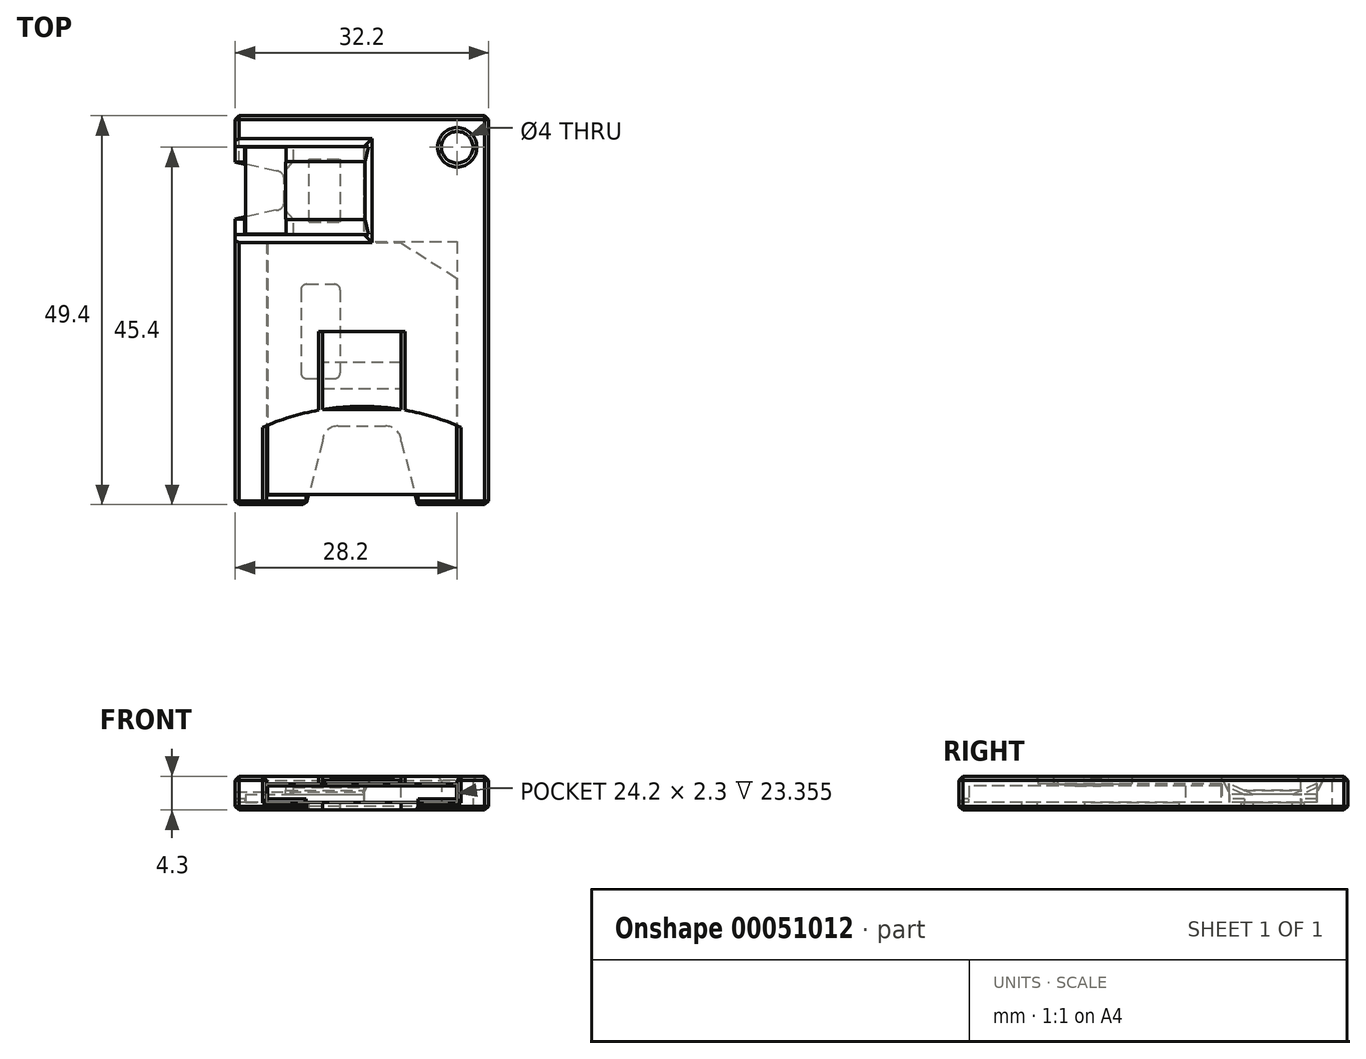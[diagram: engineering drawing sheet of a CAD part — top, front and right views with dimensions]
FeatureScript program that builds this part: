
annotation { "Feature Type Name" : "Feature", "Feature Type Description" : "" }
export const myFeature = defineFeature(function(context is Context, id is Id, definition is map)
    precondition{}
    {
        {
            var Q0;
            Q0=qCreatedBy(makeId("Top.planeOp"),FACE);
            var sketch = newSketch(context, id + "F0", { "sketchPlane" : qUnion([Q0])});
            skLineSegment(sketch, "E0.bottom", {"start": v(0, 32) * mm, "end": v(24, 32) * mm});
            skLineSegment(sketch, "E0.top", {"start": v(0, 0) * mm, "end": v(24, 0) * mm});
            skLineSegment(sketch, "E0.left", {"start": v(0, 32) * mm, "end": v(0, 0) * mm});
            skLineSegment(sketch, "E0.right", {"start": v(24, 32) * mm, "end": v(24, 0) * mm});
            skLineSegment(sketch, "E1", {"start": v(16.92, 32) * mm, "end": v(24, 27.5) * mm});
            skLineSegment(sketch, "E2.0", {"start": v(-0.1, 32.1) * mm, "end": v(-0.1, -0.1) * mm});
            skLineSegment(sketch, "E2.1", {"start": v(-0.1, 32.1) * mm, "end": v(24.1, 32.1) * mm});
            skLineSegment(sketch, "E2.2", {"start": v(24.1, 32.1) * mm, "end": v(24.1, -0.1) * mm});
            skLineSegment(sketch, "E2.3", {"start": v(-0.1, -0.1) * mm, "end": v(24.1, -0.1) * mm});
            skLineSegment(sketch, "E3.0", {"start": v(-4.1, 48.1) * mm, "end": v(28.1, 48.1) * mm});
            skLineSegment(sketch, "E3.1", {"start": v(-4.1, 48.1) * mm, "end": v(-4.1, -1.3) * mm});
            skLineSegment(sketch, "E3.3", {"start": v(28.1, 48.1) * mm, "end": v(28.1, -1.3) * mm});
            skLineSegment(sketch, "E4.0", {"start": v(-4.1, -1.3) * mm, "end": v(28.1, -1.3) * mm});
            skLineSegment(sketch, "E5", {"start": v(-0.1, -0.1) * mm, "end": v(-0.1, -1.3) * mm});
            skLineSegment(sketch, "E6", {"start": v(24.1, -0.1) * mm, "end": v(24.1, -1.3) * mm});
            skLineSegment(sketch, "E7", {"start": v(19.1, -0.1) * mm, "end": v(19.1, -1.3) * mm});
            skLineSegment(sketch, "E8", {"start": v(4.9, -0.1) * mm, "end": v(4.9, -1.3) * mm});
            skLineSegment(sketch, "E9", {"start": v(12, -1.3) * mm, "end": v(12, 48.1) * mm, "construction": true});
            skLineSegment(sketch, "E10.bottom", {"start": v(9, 8.7) * mm, "end": v(15, 8.7) * mm});
            skLineSegment(sketch, "E10.top", {"start": v(7, -1.3) * mm, "end": v(17, -1.3) * mm});
            skLineSegment(sketch, "E10.left", {"start": v(7, 6.7) * mm, "end": v(7, -1.3) * mm});
            skLineSegment(sketch, "E10.right", {"start": v(17, 6.7) * mm, "end": v(17, -1.3) * mm});
            skPoint(sketch, "E11", {"position": v(12, 8.7) * mm});
            skPoint(sketch, "E12.visualSharp", {"position": v(7, 8.7) * mm});
            skArc(sketch, "E12.filletArc", {"start": v(9, 8.7) * mm, "mid": v(7.59, 8.11) * mm, "end": v(7, 6.7) * mm});
            skPoint(sketch, "E13.visualSharp", {"position": v(17, 8.7) * mm});
            skArc(sketch, "E13.filletArc", {"start": v(17, 6.7) * mm, "mid": v(16.41, 8.11) * mm, "end": v(15, 8.7) * mm});
            skCircle(sketch, "E14", {"center": v(24.1, 44.1) * mm, "radius": 2 * mm});
            skLineSegment(sketch, "E15", {"start": v(17, 6.7) * mm, "end": v(19.1, -1.3) * mm});
            skLineSegment(sketch, "E16", {"start": v(7, 6.7) * mm, "end": v(4.9, -1.3) * mm});
            skLineSegment(sketch, "E17.bottom", {"start": v(-2.8, 44.1) * mm, "end": v(12.2, 44.1) * mm});
            skLineSegment(sketch, "E17.top", {"start": v(-2.8, 33.1) * mm, "end": v(12.2, 33.1) * mm});
            skLineSegment(sketch, "E17.left", {"start": v(-2.8, 44.1) * mm, "end": v(-2.8, 33.1) * mm});
            skLineSegment(sketch, "E17.right", {"start": v(12.2, 44.1) * mm, "end": v(12.2, 33.1) * mm});
            skLineSegment(sketch, "E18.0", {"start": v(-2.9, 44.2) * mm, "end": v(12.3, 44.2) * mm});
            skLineSegment(sketch, "E18.1", {"start": v(-2.9, 44.2) * mm, "end": v(-2.9, 33) * mm});
            skLineSegment(sketch, "E18.2", {"start": v(-2.9, 33) * mm, "end": v(12.3, 33) * mm});
            skLineSegment(sketch, "E18.3", {"start": v(12.3, 44.2) * mm, "end": v(12.3, 33) * mm});
            skLineSegment(sketch, "E19", {"start": v(-2.9, 33) * mm, "end": v(-4.1, 33) * mm});
            skLineSegment(sketch, "E20", {"start": v(-2.9, 44.2) * mm, "end": v(-4.1, 44.2) * mm});
            skLineSegment(sketch, "E21", {"start": v(-2.9, 35) * mm, "end": v(-4.1, 35) * mm});
            skLineSegment(sketch, "E22", {"start": v(-2.9, 42.2) * mm, "end": v(-4.1, 42.2) * mm});
            skLineSegment(sketch, "E23", {"start": v(12.3, 38.6) * mm, "end": v(-2.9, 38.6) * mm, "construction": true});
            skLineSegment(sketch, "E24.rect.bottom", {"start": v(-4.1, 36.1) * mm, "end": v(1.1, 36.1) * mm});
            skLineSegment(sketch, "E24.rect.top", {"start": v(-4.1, 41.1) * mm, "end": v(1.1, 41.1) * mm});
            skLineSegment(sketch, "E24.rect.left", {"start": v(-4.1, 36.1) * mm, "end": v(-4.1, 41.1) * mm});
            skLineSegment(sketch, "E24.rect.right", {"start": v(2.1, 37.1) * mm, "end": v(2.1, 40.1) * mm});
            skPoint(sketch, "E24.rect.middle", {"position": v(-1, 38.6) * mm});
            skPoint(sketch, "E25.visualSharp", {"position": v(2.1, 41.1) * mm});
            skArc(sketch, "E25.filletArc", {"start": v(2.1, 40.1) * mm, "mid": v(1.8, 40.8) * mm, "end": v(1.1, 41.1) * mm});
            skPoint(sketch, "E26.visualSharp", {"position": v(2.1, 36.1) * mm});
            skArc(sketch, "E26.filletArc", {"start": v(1.1, 36.1) * mm, "mid": v(1.8, 36.4) * mm, "end": v(2.1, 37.1) * mm});
            skLineSegment(sketch, "E27", {"start": v(1.1, 41.1) * mm, "end": v(-4.1, 42.2) * mm});
            skLineSegment(sketch, "E28", {"start": v(1.1, 36.1) * mm, "end": v(-4.1, 35) * mm});
            skLineSegment(sketch, "E29.rect.bottom", {"start": v(5.3, 34.6) * mm, "end": v(9.3, 34.6) * mm});
            skLineSegment(sketch, "E29.rect.top", {"start": v(5.3, 42.6) * mm, "end": v(9.3, 42.6) * mm});
            skLineSegment(sketch, "E29.rect.left", {"start": v(5.3, 34.6) * mm, "end": v(5.3, 42.6) * mm});
            skLineSegment(sketch, "E29.rect.right", {"start": v(9.3, 34.6) * mm, "end": v(9.3, 42.6) * mm});
            skPoint(sketch, "E29.rect.middle", {"position": v(7.3, 38.6) * mm});
            skSolve(sketch);
        }
        {
            var Q0;
            {var subQ1=sQuery(id+"F0.wireOp",EDGE,"E0.top");Q0=makeQuery(id+"F0.imprint","IMPRINT",FACE,{"disambiguationData":[TD([[makeQuery(id+"F0.imprint","IMPRINT",EDGE,{"derivedFrom":subQ1}),1.0]])]});}
            var Q1;
            Q1=makeQuery(id+"F0.imprint","IMPRINT",FACE,{"disambiguationData":[TD([[makeQuery(id+"F0.imprint","IMPRINT",EDGE,{"derivedFrom":sQuery(id+"F0.wireOp",EDGE,"E10.bottom")}),-1.0]])]});
            var Q2;
            {var subQ0=sQuery(id+"F0.wireOp",EDGE,"E16");var subQ1=sQuery(id+"F0.wireOp",EDGE,"E0.top");var subQ2=makeQuery(id+"F0.imprint","INTERSECT",VERTEX,{"derivedFrom":[subQ1,subQ0]});Q2=makeQuery(id+"F0.imprint","IMPRINT",FACE,{"disambiguationData":[TD([[makeQuery(id+"F0.imprint","IMPRINT",EDGE,{"disambiguationData":[TD([[subQ2,-1.0]])],"derivedFrom":subQ1}),1.0]])]});}
            var Q3;
            {var subQ0=sQuery(id+"F0.wireOp",EDGE,"E10.right");var subQ1=sQuery(id+"F0.wireOp",EDGE,"E0.top");var subQ2=makeQuery(id+"F0.imprint","INTERSECT",VERTEX,{"derivedFrom":[subQ1,subQ0]});Q3=makeQuery(id+"F0.imprint","IMPRINT",FACE,{"disambiguationData":[TD([[makeQuery(id+"F0.imprint","IMPRINT",EDGE,{"disambiguationData":[TD([[subQ2,-1.0]])],"derivedFrom":subQ1}),1.0]])]});}
            extrude(context, id + "F1", {"entities" : qUnion([Q0, Q1, Q2, Q3]), "depth" : 2.1 * mm});
        }
        {
            var Q0;
            Q0=makeQuery(id+"F0.imprint","IMPRINT",FACE,{"disambiguationData":[TD([[makeQuery(id+"F0.imprint","IMPRINT",EDGE,{"derivedFrom":sQuery(id+"F0.wireOp",EDGE,"E2.1")}),1.0]])]});
            extrude(context, id + "F2", {"entities" : qUnion([Q0]), "depth" : 2.3 * mm});
        }
        {
            var Q0;
            Q0=makeQuery(id+"F0.imprint","IMPRINT",FACE,{"disambiguationData":[TD([[makeQuery(id+"F0.imprint","IMPRINT",EDGE,{"derivedFrom":sQuery(id+"F0.wireOp",EDGE,"E2.1")}),1.0]])]});
            var Q1;
            {var subQ9=sQuery(id+"F0.wireOp",EDGE,"E17.bottom");Q1=makeQuery(id+"F0.imprint","IMPRINT",FACE,{"disambiguationData":[TD([[makeQuery(id+"F0.imprint","IMPRINT",EDGE,{"derivedFrom":subQ9}),1.0]])]});}
            var Q2;
            {var subQ6=sQuery(id+"F0.wireOp",EDGE,"E0.left");Q2=makeQuery(id+"F0.imprint","IMPRINT",FACE,{"disambiguationData":[TD([[makeQuery(id+"F0.imprint","IMPRINT",EDGE,{"derivedFrom":subQ6}),-1.0]])]});}
            var Q3;
            {var subQ5=sQuery(id+"F0.wireOp",EDGE,"E0.left");Q3=makeQuery(id+"F0.imprint","IMPRINT",FACE,{"disambiguationData":[TD([[makeQuery(id+"F0.imprint","IMPRINT",EDGE,{"derivedFrom":subQ5}),1.0]])]});}
            var Q4;
            {var subQ4=sQuery(id+"F0.wireOp",EDGE,"E17.bottom");Q4=makeQuery(id+"F0.imprint","IMPRINT",FACE,{"disambiguationData":[TD([[makeQuery(id+"F0.imprint","IMPRINT",EDGE,{"derivedFrom":subQ4}),-1.0]])]});}
            var Q5;
            {var subQ0=sQuery(id+"F0.wireOp",EDGE,"E19");Q5=makeQuery(id+"F0.imprint","IMPRINT",FACE,{"disambiguationData":[TD([[makeQuery(id+"F0.imprint","IMPRINT",EDGE,{"derivedFrom":subQ0}),-1.0]])]});}
            var Q6;
            {var subQ0=sQuery(id+"F0.wireOp",EDGE,"E21");Q6=makeQuery(id+"F0.imprint","IMPRINT",FACE,{"disambiguationData":[TD([[makeQuery(id+"F0.imprint","IMPRINT",EDGE,{"derivedFrom":subQ0}),-1.0]])]});}
            var Q7;
            {var subQ0=sQuery(id+"F0.wireOp",EDGE,"E22");Q7=makeQuery(id+"F0.imprint","IMPRINT",FACE,{"disambiguationData":[TD([[makeQuery(id+"F0.imprint","IMPRINT",EDGE,{"derivedFrom":subQ0}),1.0]])]});}
            var Q8;
            {var subQ0=sQuery(id+"F0.wireOp",EDGE,"E20");Q8=makeQuery(id+"F0.imprint","IMPRINT",FACE,{"disambiguationData":[TD([[makeQuery(id+"F0.imprint","IMPRINT",EDGE,{"derivedFrom":subQ0}),1.0]])]});}
            var Q9;
            {var subQ3=sQuery(id+"F0.wireOp",EDGE,"E1");Q9=makeQuery(id+"F0.imprint","IMPRINT",FACE,{"disambiguationData":[TD([[makeQuery(id+"F0.imprint","IMPRINT",EDGE,{"derivedFrom":subQ3}),1.0]])]});}
            var Q10;
            {var subQ0=sQuery(id+"F0.wireOp",EDGE,"E5");Q10=makeQuery(id+"F0.imprint","IMPRINT",FACE,{"disambiguationData":[TD([[makeQuery(id+"F0.imprint","IMPRINT",EDGE,{"derivedFrom":subQ0}),1.0]])]});}
            var Q11;
            {var subQ0=sQuery(id+"F0.wireOp",EDGE,"E8");Q11=makeQuery(id+"F0.imprint","IMPRINT",FACE,{"disambiguationData":[TD([[makeQuery(id+"F0.imprint","IMPRINT",EDGE,{"derivedFrom":subQ0}),1.0]])]});}
            var Q12;
            {var subQ0=sQuery(id+"F0.wireOp",EDGE,"E7");Q12=makeQuery(id+"F0.imprint","IMPRINT",FACE,{"disambiguationData":[TD([[makeQuery(id+"F0.imprint","IMPRINT",EDGE,{"derivedFrom":subQ0}),-1.0]])]});}
            var Q13;
            {var subQ0=sQuery(id+"F0.wireOp",EDGE,"E6");Q13=makeQuery(id+"F0.imprint","IMPRINT",FACE,{"disambiguationData":[TD([[makeQuery(id+"F0.imprint","IMPRINT",EDGE,{"derivedFrom":subQ0}),-1.0]])]});}
            extrude(context, id + "F3", {"entities" : qUnion([Q0, Q1, Q2, Q3, Q4, Q5, Q6, Q7, Q8, Q9, Q10, Q11, Q12, Q13]), "operationType" : NewBodyOperationType.ADD, "oppositeDirection" : true, "depth" : 1 * mm});
        }
        {
            var Q0;
            {var subQ0=sQuery(id+"F0.wireOp",EDGE,"E5");Q0=makeQuery(id+"F0.imprint","IMPRINT",FACE,{"disambiguationData":[TD([[makeQuery(id+"F0.imprint","IMPRINT",EDGE,{"derivedFrom":subQ0}),1.0]])]});}
            var Q1;
            {var subQ0=sQuery(id+"F0.wireOp",EDGE,"E6");Q1=makeQuery(id+"F0.imprint","IMPRINT",FACE,{"disambiguationData":[TD([[makeQuery(id+"F0.imprint","IMPRINT",EDGE,{"derivedFrom":subQ0}),-1.0]])]});}
            var Q2;
            {var subQ0=sQuery(id+"F0.wireOp",EDGE,"E19");Q2=makeQuery(id+"F0.imprint","IMPRINT",FACE,{"disambiguationData":[TD([[makeQuery(id+"F0.imprint","IMPRINT",EDGE,{"derivedFrom":subQ0}),-1.0]])]});}
            var Q3;
            {var subQ0=sQuery(id+"F0.wireOp",EDGE,"E20");Q3=makeQuery(id+"F0.imprint","IMPRINT",FACE,{"disambiguationData":[TD([[makeQuery(id+"F0.imprint","IMPRINT",EDGE,{"derivedFrom":subQ0}),1.0]])]});}
            extrude(context, id + "F4", {"entities" : qUnion([Q0, Q1, Q2, Q3]), "operationType" : NewBodyOperationType.ADD, "depth" : 0.4 * mm});
        }
        {
            var Q0;
            Q0=makeQuery(id+"F2.opExtrude","CAP_FACE",FACE,{"disambiguationData":[OSD([sQuery(id+"F0.wireOp",EDGE,"E2.1"),sQuery(id+"F0.wireOp",EDGE,"E2.0"),sQuery(id+"F0.wireOp",EDGE,"E2.2"),sQuery(id+"F0.wireOp",EDGE,"E3.0"),sQuery(id+"F0.wireOp",EDGE,"E3.1"),sQuery(id+"F0.wireOp",EDGE,"E3.3"),sQuery(id+"F0.wireOp",EDGE,"E4.0"),sQuery(id+"F0.wireOp",EDGE,"E5"),sQuery(id+"F0.wireOp",EDGE,"E6")])],"isStart":false});
            var sketch = newSketch(context, id + "F5", { "sketchPlane" : qUnion([Q0])});
            skLineSegment(sketch, "E30.bottom", {"start": v(-4.1, -1.3) * mm, "end": v(28.1, -1.3) * mm});
            skLineSegment(sketch, "E30.top", {"start": v(-4.1, 48.1) * mm, "end": v(28.1, 48.1) * mm});
            skLineSegment(sketch, "E30.left", {"start": v(-4.1, -1.3) * mm, "end": v(-4.1, 48.1) * mm});
            skLineSegment(sketch, "E30.right", {"start": v(28.1, -1.3) * mm, "end": v(28.1, 48.1) * mm});
            skLineSegment(sketch, "E31", {"start": v(12, 48.1) * mm, "end": v(12, -1.3) * mm, "construction": true});
            skArc(sketch, "E32", {"start": v(28.1, 6.7) * mm, "mid": v(12, 11.2) * mm, "end": v(-4.1, 6.7) * mm});
            skLineSegment(sketch, "E33.bottom", {"start": v(6.5, 10.7) * mm, "end": v(6.5, 10.7) * mm});
            skLineSegment(sketch, "E33.top", {"start": v(7, 20.7) * mm, "end": v(6.5, 20.7) * mm});
            skLineSegment(sketch, "E33.left", {"start": v(7, 10.7) * mm, "end": v(7, 20.7) * mm});
            skLineSegment(sketch, "E33.right", {"start": v(6.5, 10.7) * mm, "end": v(6.5, 20.7) * mm});
            skLineSegment(sketch, "E34.MirrorCS", {"start": v(17, 10.7) * mm, "end": v(17, 20.7) * mm});
            skLineSegment(sketch, "E35.MirrorCS", {"start": v(17, 20.7) * mm, "end": v(17.5, 20.7) * mm});
            skLineSegment(sketch, "E36.MirrorCS", {"start": v(17.5, 10.7) * mm, "end": v(17.5, 20.7) * mm});
            skLineSegment(sketch, "E37.MirrorCS", {"start": v(17.5, 10.7) * mm, "end": v(17.5, 10.7) * mm});
            skLineSegment(sketch, "E38", {"start": v(6.5, 10.7) * mm, "end": v(7, 10.7) * mm});
            skLineSegment(sketch, "E39.MirrorCS", {"start": v(17.5, 10.7) * mm, "end": v(17, 10.7) * mm});
            skLineSegment(sketch, "E40", {"start": v(7, 10.8) * mm, "end": v(17, 10.8) * mm});
            skSolve(sketch);
        }
        {
            var Q0;
            {var subQ11=sQuery(id+"F5.wireOp",EDGE,"E30.top");Q0=makeQuery(id+"F5.imprint","IMPRINT",FACE,{"disambiguationData":[TD([[makeQuery(id+"F5.imprint","IMPRINT",EDGE,{"derivedFrom":subQ11}),-1.0]])]});}
            var Q1;
            {var subQ11=sQuery(id+"F5.wireOp",EDGE,"E33.top");Q1=makeQuery(id+"F5.imprint","IMPRINT",FACE,{"disambiguationData":[TD([[makeQuery(id+"F5.imprint","IMPRINT",EDGE,{"derivedFrom":subQ11}),-1.0]])]});}
            var Q2;
            {var subQ0=sQuery(id+"F5.wireOp",EDGE,"E30.left");var subQ1=sQuery(id+"F5.wireOp",EDGE,"E30.bottom");var subQ2=makeQuery(id+"F5.imprint","INTERSECT",VERTEX,{"derivedFrom":[subQ1,subQ0]});var subQ5=sQuery(id+"F5.wireOp",EDGE,"E32");var subQ6=makeQuery(id+"F5.imprint","INTERSECT",VERTEX,{"derivedFrom":[subQ0,subQ5]});Q2=makeQuery(id+"F5.imprint","IMPRINT",FACE,{"disambiguationData":[TD([[makeQuery(id+"F5.imprint","IMPRINT",EDGE,{"disambiguationData":[TD([[subQ2,1.0],[subQ6,-1.0]])],"derivedFrom":subQ0}),1.0]])]});}
            var Q3;
            {var subQ0=sQuery(id+"F5.wireOp",EDGE,"E30.right");var subQ1=sQuery(id+"F5.wireOp",EDGE,"E30.bottom");var subQ2=makeQuery(id+"F5.imprint","INTERSECT",VERTEX,{"derivedFrom":[subQ1,subQ0]});Q3=makeQuery(id+"F5.imprint","IMPRINT",FACE,{"disambiguationData":[TD([[makeQuery(id+"F5.imprint","IMPRINT",EDGE,{"disambiguationData":[TD([[subQ2,1.0]])],"derivedFrom":subQ0}),-1.0]])]});}
            extrude(context, id + "F6", {"entities" : qUnion([Q0, Q1, Q2, Q3]), "operationType" : NewBodyOperationType.ADD, "depth" : 1 * mm});
        }
        {
            var Q0;
            Q0=makeQuery(id+"F6.opExtrude","SWEPT_FACE",FACE,{"disambiguationData":[OSD([sQuery(id+"F5.wireOp",EDGE,"E34.MirrorCS")])]});
            var sketch = newSketch(context, id + "F7", { "sketchPlane" : qUnion([Q0])});
            skLineSegment(sketch, "E41.0", {"start": v(10.8, 3.3) * mm, "end": v(10.8, 2.3) * mm});
            skLineSegment(sketch, "E42.0", {"start": v(10.8, 2.3) * mm, "end": v(20.7, 2.3) * mm});
            skLineSegment(sketch, "E43.0", {"start": v(20.7, 3.3) * mm, "end": v(20.7, 2.3) * mm});
            skLineSegment(sketch, "E44.0", {"start": v(10.8, 3.3) * mm, "end": v(20.7, 3.3) * mm});
            skLineSegment(sketch, "E45", {"start": v(10.8, 2.8) * mm, "end": v(20.7, 3.3) * mm});
            skLineSegment(sketch, "E46", {"start": v(10.8, 2.3) * mm, "end": v(14.76, 2) * mm});
            skLineSegment(sketch, "E47", {"start": v(14.76, 2) * mm, "end": v(20.7, 2.3) * mm});
            skSolve(sketch);
        }
        {
            var Q0;
            {var subQ0=sQuery(id+"F7.wireOp",EDGE,"E44.0");Q0=makeQuery(id+"F7.imprint","IMPRINT",FACE,{"disambiguationData":[TD([[makeQuery(id+"F7.imprint","IMPRINT",EDGE,{"derivedFrom":subQ0}),-1.0]])]});}
            extrude(context, id + "F8", {"entities" : qUnion([Q0]), "operationType" : NewBodyOperationType.REMOVE, "endBound" : BoundingType.UP_TO_NEXT, "oppositeDirection" : true, "depth" : 25 * mm});
        }
        {
            var Q0;
            Q0=makeQuery(id+"F7.imprint","IMPRINT",FACE,{"disambiguationData":[TD([[makeQuery(id+"F7.imprint","IMPRINT",EDGE,{"derivedFrom":sQuery(id+"F7.wireOp",EDGE,"E42.0")}),-1.0]])]});
            var Q1;
            Q1=makeQuery(id+"F2.opExtrude","SWEPT_BODY",BODY,{"disambiguationData":[OSD([sQuery(id+"F0.wireOp",EDGE,"E2.1"),sQuery(id+"F0.wireOp",EDGE,"E2.0"),sQuery(id+"F0.wireOp",EDGE,"E2.2"),sQuery(id+"F0.wireOp",EDGE,"E3.0"),sQuery(id+"F0.wireOp",EDGE,"E3.1"),sQuery(id+"F0.wireOp",EDGE,"E3.3"),sQuery(id+"F0.wireOp",EDGE,"E4.0"),sQuery(id+"F0.wireOp",EDGE,"E5"),sQuery(id+"F0.wireOp",EDGE,"E6")])]});
            extrude(context, id + "F9", {"entities" : qUnion([Q0]), "operationType" : NewBodyOperationType.ADD, "oppositeDirection" : true, "endBoundEntityBody" : qUnion([Q1]), "depth" : 10 * mm});
        }
        {
            var Q0;
            {var subQ4=sQuery(id+"F0.wireOp",EDGE,"E17.bottom");Q0=makeQuery(id+"F0.imprint","IMPRINT",FACE,{"disambiguationData":[TD([[makeQuery(id+"F0.imprint","IMPRINT",EDGE,{"derivedFrom":subQ4}),-1.0]])]});}
            var Q1;
            {var subQ0=sQuery(id+"F0.wireOp",EDGE,"E27");var subQ1=sQuery(id+"F0.wireOp",EDGE,"E17.left");var subQ2=makeQuery(id+"F0.imprint","INTERSECT",VERTEX,{"derivedFrom":[subQ1,subQ0]});Q1=makeQuery(id+"F0.imprint","IMPRINT",FACE,{"disambiguationData":[TD([[makeQuery(id+"F0.imprint","IMPRINT",EDGE,{"disambiguationData":[TD([[subQ2,-1.0]])],"derivedFrom":subQ1}),1.0]])]});}
            var Q2;
            {var subQ0=sQuery(id+"F0.wireOp",EDGE,"E24.rect.bottom");var subQ1=sQuery(id+"F0.wireOp",EDGE,"E17.left");var subQ2=makeQuery(id+"F0.imprint","INTERSECT",VERTEX,{"derivedFrom":[subQ1,subQ0]});Q2=makeQuery(id+"F0.imprint","IMPRINT",FACE,{"disambiguationData":[TD([[makeQuery(id+"F0.imprint","IMPRINT",EDGE,{"disambiguationData":[TD([[subQ2,-1.0]])],"derivedFrom":subQ1}),1.0]])]});}
            var Q3;
            Q3=makeQuery(id+"F0.imprint","IMPRINT",FACE,{"disambiguationData":[TD([[makeQuery(id+"F0.imprint","IMPRINT",EDGE,{"derivedFrom":sQuery(id+"F0.wireOp",EDGE,"E24.rect.right")}),1.0]])]});
            var Q4;
            Q4=makeQuery(id+"F0.imprint","IMPRINT",FACE,{"disambiguationData":[TD([[makeQuery(id+"F0.imprint","IMPRINT",EDGE,{"derivedFrom":sQuery(id+"F0.wireOp",EDGE,"E29.rect.bottom")}),1.0]])]});
            extrude(context, id + "F10", {"entities" : qUnion([Q0, Q1, Q2, Q3, Q4]), "depth" : 1 * mm});
        }
        {
            var Q0;
            {var subQ0=sQuery(id+"F0.wireOp",EDGE,"E13.filletArc");var subQ1=sQuery(id+"F0.wireOp",EDGE,"E10.bottom");var subQ2=sQuery(id+"F0.wireOp",EDGE,"E4.0");var subQ3=sQuery(id+"F0.wireOp",EDGE,"E3.3");var subQ7=sQuery(id+"F0.wireOp",EDGE,"E15");var subQ10=sQuery(id+"F0.wireOp",EDGE,"E16");var subQ11=sQuery(id+"F0.wireOp",EDGE,"E3.1");var subQ13=sQuery(id+"F0.wireOp",EDGE,"E12.filletArc");Q0=makeQuery(id+"F3.boolean.opBoolean","SPLIT",FACE,{"disambiguationData":[TD([makeQuery(id+"F2.opExtrude","SWEPT_FACE",FACE,{"disambiguationData":[OSD([sQuery(id+"F0.wireOp",EDGE,"E2.1")])]})])],"derivedFrom":makeQuery(id+"F3.opExtrude","CAP_FACE",FACE,{"disambiguationData":[OSD([sQuery(id+"F0.wireOp",EDGE,"E3.0"),subQ11,subQ3,subQ2,subQ1,subQ13,subQ0,sQuery(id+"F0.wireOp",EDGE,"E14"),subQ7,subQ10,sQuery(id+"F0.wireOp",EDGE,"E24.rect.right"),sQuery(id+"F0.wireOp",EDGE,"E25.filletArc"),sQuery(id+"F0.wireOp",EDGE,"E26.filletArc"),sQuery(id+"F0.wireOp",EDGE,"E27"),sQuery(id+"F0.wireOp",EDGE,"E28")])],"isStart":true})});}
            var sketch = newSketch(context, id + "F11", { "sketchPlane" : qUnion([Q0])});
            skLineSegment(sketch, "E48.0", {"start": v(7, 20.7) * mm, "end": v(6.5, 20.7) * mm});
            skLineSegment(sketch, "E49.rect.bottom", {"start": v(8.5, 14.7) * mm, "end": v(5, 14.7) * mm});
            skLineSegment(sketch, "E49.rect.top", {"start": v(8.5, 26.7) * mm, "end": v(5, 26.7) * mm});
            skLineSegment(sketch, "E49.rect.left", {"start": v(9.25, 15.45) * mm, "end": v(9.25, 25.97) * mm});
            skLineSegment(sketch, "E49.rect.right", {"start": v(4.25, 15.45) * mm, "end": v(4.25, 25.97) * mm});
            skPoint(sketch, "E49.rect.middle", {"position": v(6.75, 20.7) * mm});
            skPoint(sketch, "E50.visualSharp", {"position": v(4.25, 26.7) * mm});
            skArc(sketch, "E50.filletArc", {"start": v(5, 26.7) * mm, "mid": v(4.47, 26.5) * mm, "end": v(4.25, 25.97) * mm});
            skPoint(sketch, "E51.visualSharp", {"position": v(9.25, 26.7) * mm});
            skArc(sketch, "E51.filletArc", {"start": v(9.25, 25.97) * mm, "mid": v(9.03, 26.5) * mm, "end": v(8.5, 26.7) * mm});
            skPoint(sketch, "E52.visualSharp", {"position": v(9.25, 14.7) * mm});
            skArc(sketch, "E52.filletArc", {"start": v(8.5, 14.7) * mm, "mid": v(9.03, 14.93) * mm, "end": v(9.25, 15.45) * mm});
            skPoint(sketch, "E53.visualSharp", {"position": v(4.25, 14.7) * mm});
            skArc(sketch, "E53.filletArc", {"start": v(4.25, 15.45) * mm, "mid": v(4.47, 14.93) * mm, "end": v(5, 14.7) * mm});
            skLineSegment(sketch, "E54.MirrorCS", {"start": v(14.75, 15.45) * mm, "end": v(14.75, 25.97) * mm});
            skArc(sketch, "E55.MirrorCS", {"start": v(14.75, 25.97) * mm, "mid": v(14.97, 26.5) * mm, "end": v(15.5, 26.7) * mm});
            skArc(sketch, "E56.MirrorCS", {"start": v(19, 26.7) * mm, "mid": v(19.53, 26.5) * mm, "end": v(19.75, 25.97) * mm});
            skLineSegment(sketch, "E57.MirrorCS", {"start": v(17, 20.7) * mm, "end": v(17.5, 20.7) * mm});
            skPoint(sketch, "E58.MirrorP", {"position": v(19.75, 14.7) * mm});
            skPoint(sketch, "E59.MirrorP", {"position": v(14.75, 26.7) * mm});
            skPoint(sketch, "E60.MirrorP", {"position": v(14.75, 14.7) * mm});
            skArc(sketch, "E61.MirrorCS", {"start": v(15.5, 14.7) * mm, "mid": v(14.97, 14.93) * mm, "end": v(14.75, 15.45) * mm});
            skArc(sketch, "E62.MirrorCS", {"start": v(19.75, 15.45) * mm, "mid": v(19.53, 14.93) * mm, "end": v(19, 14.7) * mm});
            skPoint(sketch, "E63.MirrorP", {"position": v(19.75, 26.7) * mm});
            skPoint(sketch, "E64.MirrorP", {"position": v(17.25, 20.7) * mm});
            skLineSegment(sketch, "E65.MirrorCS", {"start": v(15.5, 14.7) * mm, "end": v(19, 14.7) * mm});
            skLineSegment(sketch, "E66.MirrorCS", {"start": v(15.5, 26.7) * mm, "end": v(19, 26.7) * mm});
            skLineSegment(sketch, "E67.MirrorCS", {"start": v(19.75, 15.45) * mm, "end": v(19.75, 25.97) * mm});
            skSolve(sketch);
        }
        {
            var Q0;
            Q0=makeQuery(id+"F11.imprint","IMPRINT",FACE,{"disambiguationData":[TD([[makeQuery(id+"F11.imprint","IMPRINT",EDGE,{"derivedFrom":sQuery(id+"F11.wireOp",EDGE,"E49.rect.bottom")}),-1.0]])]});
            var Q1;
            Q1=makeQuery(id+"F11.imprint","IMPRINT",FACE,{"disambiguationData":[TD([[makeQuery(id+"F11.imprint","IMPRINT",EDGE,{"derivedFrom":sQuery(id+"F11.wireOp",EDGE,"E56.MirrorCS")}),-1.0]])]});
            extrude(context, id + "F12", {"entities" : qUnion([Q0, Q1]), "operationType" : NewBodyOperationType.REMOVE, "endBound" : BoundingType.UP_TO_NEXT, "oppositeDirection" : true, "depth" : 25 * mm});
        }
        {
            var Q0;
            {var subQ0=sQuery(id+"F0.wireOp",EDGE,"E18.3");Q0=makeQuery(id+"F6.boolean.opBoolean","MERGE",FACE,{"derivedFrom":[makeQuery(id+"F2.opExtrude","SWEPT_FACE",FACE,{"disambiguationData":[OSD([subQ0])]}),makeQuery(id+"F6.opExtrude","SWEPT_FACE",FACE,{"disambiguationData":[OSD([subQ0])]})]});}
            var sketch = newSketch(context, id + "F13", { "sketchPlane" : qUnion([Q0])});
            skLineSegment(sketch, "E68.0", {"start": v(-44.2, 3.3) * mm, "end": v(-44.2, 0) * mm});
            skLineSegment(sketch, "E69.0", {"start": v(-33, 3.3) * mm, "end": v(-33, 0) * mm});
            skLineSegment(sketch, "E69.1", {"start": v(-44.1, 0) * mm, "end": v(-33.1, 0) * mm});
            skLineSegment(sketch, "E69.2", {"start": v(-44.2, 3.3) * mm, "end": v(-33, 3.3) * mm});
            skLineSegment(sketch, "E70.0", {"start": v(-44.2, 0) * mm, "end": v(-33, 0) * mm});
            skLineSegment(sketch, "E71", {"start": v(-44.2, 1.88) * mm, "end": v(-42.3, 1) * mm});
            skLineSegment(sketch, "E72", {"start": v(-42.3, 1) * mm, "end": v(-34.9, 1) * mm});
            skLineSegment(sketch, "E73", {"start": v(-34.9, 1) * mm, "end": v(-33, 1.88) * mm});
            skLineSegment(sketch, "E74", {"start": v(-38.6, 3.3) * mm, "end": v(-38.6, 0) * mm, "construction": true});
            skLineSegment(sketch, "E75", {"start": v(-44.2, 2.38) * mm, "end": v(-42.3, 1.5) * mm});
            skLineSegment(sketch, "E76", {"start": v(-42.3, 1.5) * mm, "end": v(-34.9, 1.5) * mm});
            skLineSegment(sketch, "E77", {"start": v(-34.9, 1.5) * mm, "end": v(-33, 2.38) * mm});
            skSolve(sketch);
        }
        {
            var Q0;
            {var subQ0=sQuery(id+"F13.wireOp",EDGE,"E71");Q0=makeQuery(id+"F13.imprint","IMPRINT",FACE,{"disambiguationData":[TD([[makeQuery(id+"F13.imprint","IMPRINT",EDGE,{"derivedFrom":subQ0}),1.0]])]});}
            extrude(context, id + "F14", {"entities" : qUnion([Q0]), "operationType" : NewBodyOperationType.ADD, "depth" : 10 * mm});
        }
        {
            var Q0;
            Q0=makeQuery(id+"F14.opExtrude","CAP_EDGE",EDGE,{"disambiguationData":[OSD([sQuery(id+"F13.wireOp",EDGE,"E71")])],"isStart":false});
            var Q1;
            Q1=makeQuery(id+"F14.opExtrude","CAP_EDGE",EDGE,{"disambiguationData":[OSD([sQuery(id+"F13.wireOp",EDGE,"E72")])],"isStart":false});
            var Q2;
            Q2=makeQuery(id+"F14.opExtrude","CAP_EDGE",EDGE,{"disambiguationData":[OSD([sQuery(id+"F13.wireOp",EDGE,"E73")])],"isStart":false});
            chamfer(context, id + "F15", {"entities" : qUnion([Q0, Q1, Q2]), "chamferType" : ChamferType.TWO_OFFSETS, "width1" : 0.5 * mm, "oppositeDirection" : false, "width2" : 1 * mm, "tangentPropagation" : true});
        }
        {
            var Q0;
            Q0=makeQuery(id+"F6.opExtrude","CAP_EDGE",EDGE,{"disambiguationData":[OSD([sQuery(id+"F0.wireOp",EDGE,"E18.2"),sQuery(id+"F0.wireOp",EDGE,"E19")])],"isStart":false});
            var Q1;
            Q1=makeQuery(id+"F6.opExtrude","CAP_EDGE",EDGE,{"disambiguationData":[OSD([sQuery(id+"F0.wireOp",EDGE,"E18.0"),sQuery(id+"F0.wireOp",EDGE,"E20")])],"isStart":false});
            var Q2;
            Q2=makeQuery(id+"F6.opExtrude","CAP_EDGE",EDGE,{"disambiguationData":[OSD([sQuery(id+"F0.wireOp",EDGE,"E18.3")])],"isStart":false});
            chamfer(context, id + "F16", {"entities" : qUnion([Q0, Q1, Q2]), "chamferType" : ChamferType.TWO_OFFSETS, "width1" : 1 * mm, "oppositeDirection" : false, "width2" : 2 * mm, "tangentPropagation" : true});
        }
        {
            var Q0;
            {var subQ0=sQuery(id+"F5.wireOp",EDGE,"E30.bottom");Q0=makeQuery(id+"F6.opExtrude","CAP_EDGE",EDGE,{"disambiguationData":[OSD([subQ0]),TDD([makeQuery(id+"F5.imprint","IMPRINT",EDGE,{"disambiguationData":[TD([[makeQuery(id+"F5.imprint","INTERSECT",VERTEX,{"derivedFrom":[subQ0,sQuery(id+"F5.wireOp",EDGE,"E30.left")]}),-1.0]])],"derivedFrom":subQ0})])],"isStart":false});}
            var Q1;
            {var subQ0=sQuery(id+"F5.wireOp",EDGE,"E30.bottom");Q1=makeQuery(id+"F6.opExtrude","CAP_EDGE",EDGE,{"disambiguationData":[OSD([subQ0]),TDD([makeQuery(id+"F5.imprint","IMPRINT",EDGE,{"disambiguationData":[TD([[makeQuery(id+"F5.imprint","INTERSECT",VERTEX,{"derivedFrom":[subQ0,sQuery(id+"F5.wireOp",EDGE,"E30.right")]}),1.0]])],"derivedFrom":subQ0})])],"isStart":false});}
            var Q2;
            {var subQ0=sQuery(id+"F0.wireOp",EDGE,"E4.0");Q2=makeQuery(id+"F4.opExtrude","CAP_EDGE",EDGE,{"disambiguationData":[OSD([subQ0]),TDD([makeQuery(id+"F0.imprint","IMPRINT",EDGE,{"disambiguationData":[TD([[makeQuery(id+"F0.imprint","INTERSECT",VERTEX,{"derivedFrom":[subQ0,sQuery(id+"F0.wireOp",EDGE,"E5")]}),-1.0]])],"derivedFrom":subQ0})])],"isStart":false});}
            var Q3;
            Q3=makeQuery(id+"F6.opExtrude","CAP_EDGE",EDGE,{"disambiguationData":[OSD([sQuery(id+"F0.wireOp",EDGE,"E2.0"),sQuery(id+"F0.wireOp",EDGE,"E5")])],"isStart":false});
            var Q4;
            Q4=makeQuery(id+"F6.opExtrude","CAP_EDGE",EDGE,{"disambiguationData":[OSD([sQuery(id+"F0.wireOp",EDGE,"E2.2"),sQuery(id+"F0.wireOp",EDGE,"E6")])],"isStart":false});
            var Q5;
            {var subQ0=sQuery(id+"F0.wireOp",EDGE,"E6");Q5=makeQuery(id+"F6.boolean.opBoolean","MERGE",EDGE,{"derivedFrom":[makeQuery(id+"F2.opExtrude","SWEPT_EDGE",EDGE,{"disambiguationData":[OSD([sQuery(id+"F0.wireOp",EDGE,"E4.0"),subQ0])]}),makeQuery(id+"F6.opExtrude","SWEPT_EDGE",EDGE,{"disambiguationData":[OSD([sQuery(id+"F0.wireOp",EDGE,"E2.2"),subQ0,sQuery(id+"F5.wireOp",EDGE,"E30.bottom")])]})]});}
            var Q6;
            {var subQ0=sQuery(id+"F0.wireOp",EDGE,"E4.0");Q6=makeQuery(id+"F4.opExtrude","CAP_EDGE",EDGE,{"disambiguationData":[OSD([subQ0]),TDD([makeQuery(id+"F0.imprint","IMPRINT",EDGE,{"disambiguationData":[TD([[makeQuery(id+"F0.imprint","INTERSECT",VERTEX,{"derivedFrom":[subQ0,sQuery(id+"F0.wireOp",EDGE,"E6")]}),1.0]])],"derivedFrom":subQ0})])],"isStart":false});}
            var Q7;
            Q7=makeQuery(id+"F3.opExtrude","SWEPT_EDGE",EDGE,{"disambiguationData":[OSD([sQuery(id+"F0.wireOp",EDGE,"E4.0"),sQuery(id+"F0.wireOp",EDGE,"E8"),sQuery(id+"F0.wireOp",EDGE,"E16")])]});
            var Q8;
            {var subQ0=sQuery(id+"F0.wireOp",EDGE,"E5");Q8=makeQuery(id+"F6.boolean.opBoolean","MERGE",EDGE,{"derivedFrom":[makeQuery(id+"F2.opExtrude","SWEPT_EDGE",EDGE,{"disambiguationData":[OSD([sQuery(id+"F0.wireOp",EDGE,"E4.0"),subQ0])]}),makeQuery(id+"F6.opExtrude","SWEPT_EDGE",EDGE,{"disambiguationData":[OSD([sQuery(id+"F0.wireOp",EDGE,"E2.0"),subQ0,sQuery(id+"F5.wireOp",EDGE,"E30.bottom")])]})]});}
            var Q9;
            Q9=makeQuery(id+"F6.opExtrude","CAP_EDGE",EDGE,{"disambiguationData":[OSD([sQuery(id+"F5.wireOp",EDGE,"E30.right")])],"isStart":false});
            var Q10;
            {var subQ0=sQuery(id+"F0.wireOp",EDGE,"E4.0");var subQ1=sQuery(id+"F0.wireOp",EDGE,"E3.3");Q10=makeQuery(id+"F6.boolean.opBoolean","MERGE",EDGE,{"derivedFrom":[makeQuery(id+"F3.boolean.opBoolean","MERGE",EDGE,{"derivedFrom":[makeQuery(id+"F2.opExtrude","SWEPT_EDGE",EDGE,{"disambiguationData":[OSD([subQ1,subQ0])]}),makeQuery(id+"F3.opExtrude","SWEPT_EDGE",EDGE,{"disambiguationData":[OSD([subQ1,subQ0])]})]}),makeQuery(id+"F6.opExtrude","SWEPT_EDGE",EDGE,{"disambiguationData":[OSD([sQuery(id+"F5.wireOp",EDGE,"E30.bottom"),sQuery(id+"F5.wireOp",EDGE,"E30.right")])]})]});}
            var Q11;
            {var subQ0=sQuery(id+"F0.wireOp",EDGE,"E4.0");var subQ1=sQuery(id+"F0.wireOp",EDGE,"E3.1");Q11=makeQuery(id+"F6.boolean.opBoolean","MERGE",EDGE,{"derivedFrom":[makeQuery(id+"F3.boolean.opBoolean","MERGE",EDGE,{"derivedFrom":[makeQuery(id+"F2.opExtrude","SWEPT_EDGE",EDGE,{"disambiguationData":[OSD([subQ1,subQ0])]}),makeQuery(id+"F3.opExtrude","SWEPT_EDGE",EDGE,{"disambiguationData":[OSD([subQ1,subQ0])]})]}),makeQuery(id+"F6.opExtrude","SWEPT_EDGE",EDGE,{"disambiguationData":[OSD([sQuery(id+"F5.wireOp",EDGE,"E30.bottom"),sQuery(id+"F5.wireOp",EDGE,"E30.left")])]})]});}
            var Q12;
            {var subQ0=sQuery(id+"F5.wireOp",EDGE,"E30.left");var subQ1=makeQuery(id+"F5.imprint","INTERSECT",VERTEX,{"derivedFrom":[subQ0,sQuery(id+"F5.wireOp",EDGE,"E32")]});Q12=makeQuery(id+"F6.opExtrude","CAP_EDGE",EDGE,{"disambiguationData":[OSD([subQ0]),TDD([makeQuery(id+"F5.imprint","IMPRINT",EDGE,{"disambiguationData":[TD([[makeQuery(id+"F5.imprint","INTERSECT",VERTEX,{"derivedFrom":[makeQuery(id+"F2.opExtrude","CAP_EDGE",EDGE,{"disambiguationData":[OSD([sQuery(id+"F0.wireOp",EDGE,"E18.2"),sQuery(id+"F0.wireOp",EDGE,"E19")])],"isStart":false}),subQ0]}),-1.0],[subQ1,1.0]])],"derivedFrom":subQ0}),makeQuery(id+"F5.imprint","IMPRINT",EDGE,{"disambiguationData":[TD([[makeQuery(id+"F5.imprint","INTERSECT",VERTEX,{"derivedFrom":[sQuery(id+"F5.wireOp",EDGE,"E30.bottom"),subQ0]}),1.0],[subQ1,-1.0]])],"derivedFrom":subQ0})])],"isStart":false});}
            var Q13;
            Q13=makeQuery(id+"F6.opExtrude","CAP_EDGE",EDGE,{"disambiguationData":[OSD([sQuery(id+"F0.wireOp",EDGE,"E14")])],"isStart":false});
            var Q14;
            Q14=makeQuery(id+"F3.opExtrude","CAP_EDGE",EDGE,{"disambiguationData":[OSD([sQuery(id+"F0.wireOp",EDGE,"E14")])],"isStart":false});
            var Q15;
            Q15=makeQuery(id+"F6.opExtrude","CAP_EDGE",EDGE,{"disambiguationData":[OSD([sQuery(id+"F5.wireOp",EDGE,"E30.top")])],"isStart":false});
            var Q16;
            {var subQ0=sQuery(id+"F5.wireOp",EDGE,"E30.left");Q16=makeQuery(id+"F6.opExtrude","CAP_EDGE",EDGE,{"disambiguationData":[OSD([subQ0]),TDD([makeQuery(id+"F5.imprint","IMPRINT",EDGE,{"disambiguationData":[TD([[makeQuery(id+"F5.imprint","INTERSECT",VERTEX,{"derivedFrom":[sQuery(id+"F5.wireOp",EDGE,"E30.top"),subQ0]}),-1.0],[makeQuery(id+"F5.imprint","INTERSECT",VERTEX,{"derivedFrom":[makeQuery(id+"F2.opExtrude","CAP_EDGE",EDGE,{"disambiguationData":[OSD([sQuery(id+"F0.wireOp",EDGE,"E18.0"),sQuery(id+"F0.wireOp",EDGE,"E20")])],"isStart":false}),subQ0]}),1.0]])],"derivedFrom":subQ0})])],"isStart":false});}
            var Q17;
            {var subQ0=sQuery(id+"F0.wireOp",EDGE,"E3.1");var subQ1=makeQuery(id+"F0.imprint","INTERSECT",VERTEX,{"derivedFrom":[subQ0,sQuery(id+"F0.wireOp",EDGE,"E19")]});Q17=makeQuery(id+"F3.opExtrude","CAP_EDGE",EDGE,{"disambiguationData":[OSD([subQ0]),TDD([makeQuery(id+"F0.imprint","IMPRINT",EDGE,{"disambiguationData":[TD([[subQ1,1.0]])],"derivedFrom":subQ0}),makeQuery(id+"F0.imprint","IMPRINT",EDGE,{"disambiguationData":[TD([[makeQuery(id+"F0.imprint","INTERSECT",VERTEX,{"derivedFrom":[subQ0,sQuery(id+"F0.wireOp",EDGE,"E4.0")]}),1.0]])],"derivedFrom":subQ0})])],"isStart":false});}
            var Q18;
            Q18=makeQuery(id+"F3.opExtrude","CAP_EDGE",EDGE,{"disambiguationData":[OSD([sQuery(id+"F0.wireOp",EDGE,"E3.3")])],"isStart":false});
            var Q19;
            Q19=makeQuery(id+"F3.opExtrude","CAP_EDGE",EDGE,{"disambiguationData":[OSD([sQuery(id+"F0.wireOp",EDGE,"E3.0")])],"isStart":false});
            var Q20;
            {var subQ0=sQuery(id+"F0.wireOp",EDGE,"E3.3");var subQ1=sQuery(id+"F0.wireOp",EDGE,"E3.0");Q20=makeQuery(id+"F6.boolean.opBoolean","MERGE",EDGE,{"derivedFrom":[makeQuery(id+"F3.boolean.opBoolean","MERGE",EDGE,{"derivedFrom":[makeQuery(id+"F2.opExtrude","SWEPT_EDGE",EDGE,{"disambiguationData":[OSD([subQ1,subQ0])]}),makeQuery(id+"F3.opExtrude","SWEPT_EDGE",EDGE,{"disambiguationData":[OSD([subQ1,subQ0])]})]}),makeQuery(id+"F6.opExtrude","SWEPT_EDGE",EDGE,{"disambiguationData":[OSD([sQuery(id+"F5.wireOp",EDGE,"E30.top"),sQuery(id+"F5.wireOp",EDGE,"E30.right")])]})]});}
            var Q21;
            {var subQ0=sQuery(id+"F0.wireOp",EDGE,"E3.1");var subQ1=sQuery(id+"F0.wireOp",EDGE,"E3.0");Q21=makeQuery(id+"F6.boolean.opBoolean","MERGE",EDGE,{"derivedFrom":[makeQuery(id+"F3.boolean.opBoolean","MERGE",EDGE,{"derivedFrom":[makeQuery(id+"F2.opExtrude","SWEPT_EDGE",EDGE,{"disambiguationData":[OSD([subQ1,subQ0])]}),makeQuery(id+"F3.opExtrude","SWEPT_EDGE",EDGE,{"disambiguationData":[OSD([subQ1,subQ0])]})]}),makeQuery(id+"F6.opExtrude","SWEPT_EDGE",EDGE,{"disambiguationData":[OSD([sQuery(id+"F5.wireOp",EDGE,"E30.top"),sQuery(id+"F5.wireOp",EDGE,"E30.left")])]})]});}
            var Q22;
            {var subQ0=sQuery(id+"F0.wireOp",EDGE,"E3.1");var subQ1=makeQuery(id+"F0.imprint","INTERSECT",VERTEX,{"derivedFrom":[subQ0,sQuery(id+"F0.wireOp",EDGE,"E20")]});Q22=makeQuery(id+"F3.opExtrude","CAP_EDGE",EDGE,{"disambiguationData":[OSD([subQ0]),TDD([makeQuery(id+"F0.imprint","IMPRINT",EDGE,{"disambiguationData":[TD([[makeQuery(id+"F0.imprint","INTERSECT",VERTEX,{"derivedFrom":[sQuery(id+"F0.wireOp",EDGE,"E3.0"),subQ0]}),-1.0]])],"derivedFrom":subQ0}),makeQuery(id+"F0.imprint","IMPRINT",EDGE,{"disambiguationData":[TD([[subQ1,-1.0]])],"derivedFrom":subQ0})])],"isStart":false});}
            var Q23;
            {var subQ0=sQuery(id+"F0.wireOp",EDGE,"E4.0");var subQ1=makeQuery(id+"F0.imprint","INTERSECT",VERTEX,{"derivedFrom":[subQ0,sQuery(id+"F0.wireOp",EDGE,"E5")]});Q23=makeQuery(id+"F3.opExtrude","CAP_EDGE",EDGE,{"disambiguationData":[OSD([subQ0]),TDD([makeQuery(id+"F0.imprint","IMPRINT",EDGE,{"disambiguationData":[TD([[makeQuery(id+"F0.imprint","INTERSECT",VERTEX,{"derivedFrom":[sQuery(id+"F0.wireOp",EDGE,"E3.1"),subQ0]}),-1.0]])],"derivedFrom":subQ0}),makeQuery(id+"F0.imprint","IMPRINT",EDGE,{"disambiguationData":[TD([[subQ1,-1.0]])],"derivedFrom":subQ0})])],"isStart":false});}
            var Q24;
            {var subQ0=sQuery(id+"F0.wireOp",EDGE,"E4.0");var subQ1=makeQuery(id+"F0.imprint","INTERSECT",VERTEX,{"derivedFrom":[subQ0,sQuery(id+"F0.wireOp",EDGE,"E6")]});Q24=makeQuery(id+"F3.opExtrude","CAP_EDGE",EDGE,{"disambiguationData":[OSD([subQ0]),TDD([makeQuery(id+"F0.imprint","IMPRINT",EDGE,{"disambiguationData":[TD([[subQ1,1.0]])],"derivedFrom":subQ0}),makeQuery(id+"F0.imprint","IMPRINT",EDGE,{"disambiguationData":[TD([[makeQuery(id+"F0.imprint","INTERSECT",VERTEX,{"derivedFrom":[sQuery(id+"F0.wireOp",EDGE,"E3.3"),subQ0]}),1.0]])],"derivedFrom":subQ0})])],"isStart":false});}
            chamfer(context, id + "F17", {"entities" : qUnion([Q0, Q1, Q2, Q3, Q4, Q5, Q6, Q7, Q8, Q9, Q10, Q11, Q12, Q13, Q14, Q15, Q16, Q17, Q18, Q19, Q20, Q21, Q22, Q23, Q24]), "width" : 0.5 * mm, "tangentPropagation" : true});
        }
    });
